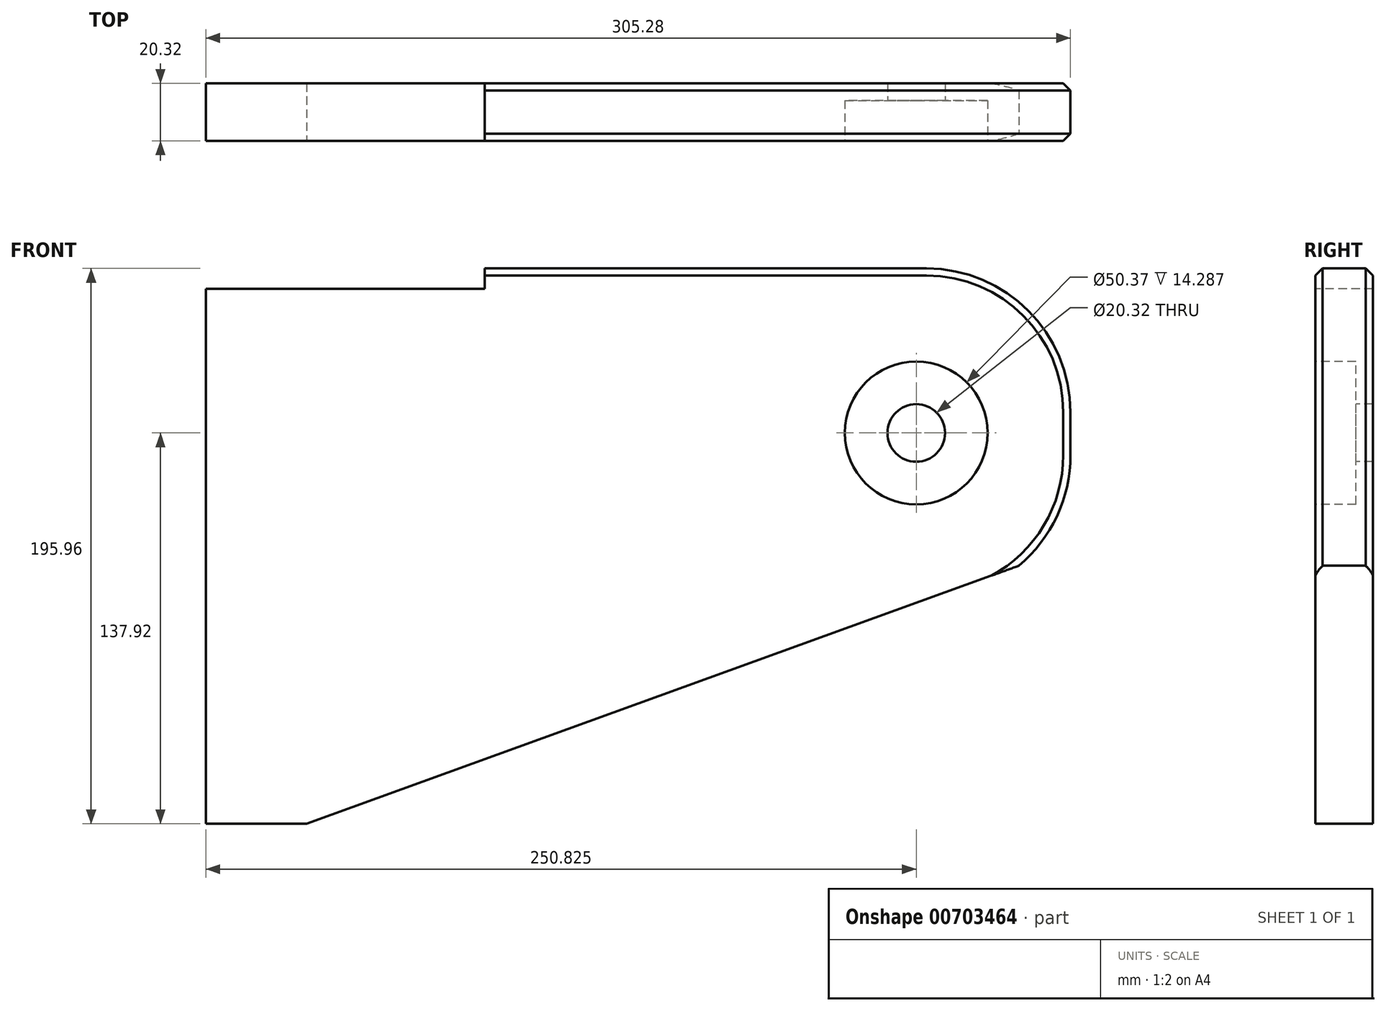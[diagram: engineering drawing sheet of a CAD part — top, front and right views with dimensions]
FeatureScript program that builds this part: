
annotation { "Feature Type Name" : "Feature", "Feature Type Description" : "" }
export const myFeature = defineFeature(function(context is Context, id is Id, definition is map)
    precondition{}
    {
        {
            var Q0;
            Q0=qCreatedBy(makeId("Front.planeOp"),FACE);
            var sketch = newSketch(context, id + "F0", { "sketchPlane" : qUnion([Q0])});
            skLineSegment(sketch, "E0", {"start": v(0, 0) * mm, "end": v(0, -188.72) * mm});
            skLineSegment(sketch, "E1", {"start": v(0, 0) * mm, "end": v(98.43, 0) * mm});
            skLineSegment(sketch, "E2", {"start": v(98.43, 0) * mm, "end": v(98.43, 7.24) * mm});
            skPoint(sketch, "E3", {"position": v(250.83, -50.8) * mm});
            skLineSegment(sketch, "E4", {"start": v(98.43, 7.24) * mm, "end": v(152.88, 7.24) * mm});
            skLineSegment(sketch, "E5", {"start": v(0, -188.72) * mm, "end": v(35.54, -188.72) * mm});
            skCircle(sketch, "E6", {"center": v(250.83, -50.8) * mm, "radius": 25.18 * mm});
            skCircle(sketch, "E7", {"center": v(250.83, -50.8) * mm, "radius": 10.16 * mm});
            skPoint(sketch, "E8.visualSharp", {"position": v(305.28, 7.24) * mm});
            skPoint(sketch, "E9.visualSharp", {"position": v(314.33, -98.03) * mm});
            skLineSegment(sketch, "E10", {"start": v(254.48, 7.24) * mm, "end": v(254.48, 7.24) * mm});
            skLineSegment(sketch, "E11", {"start": v(305.28, -43.56) * mm, "end": v(305.28, -58.64) * mm});
            skLineSegment(sketch, "E12", {"start": v(254.48, -109.44) * mm, "end": v(254.48, -109.44) * mm});
            skPoint(sketch, "E13.visualSharp", {"position": v(305.28, -109.44) * mm});
            skArc(sketch, "E13.filletArc", {"start": v(287, -97.67) * mm, "mid": v(300.48, -80.19) * mm, "end": v(305.28, -58.64) * mm});
            skArc(sketch, "E14.filletArc", {"start": v(305.28, -43.56) * mm, "mid": v(290.4, -7.64) * mm, "end": v(254.48, 7.24) * mm});
            skLineSegment(sketch, "E15", {"start": v(152.88, 7.24) * mm, "end": v(254.48, 7.24) * mm});
            skLineSegment(sketch, "E16", {"start": v(254.48, -109.44) * mm, "end": v(35.54, -188.72) * mm});
            skLineSegment(sketch, "E17", {"start": v(254.48, -109.44) * mm, "end": v(287, -97.67) * mm});
            skPoint(sketch, "E17.endSnap0", {"position": v(290.4, -94.56) * mm});
            skPoint(sketch, "E18.orphan", {"position": v(295.57, -94.56) * mm});
            skSolve(sketch);
        }
        {
            var Q0;
            Q0=makeQuery(id+"F0.imprint","IMPRINT",FACE,{"disambiguationData":[TD([[makeQuery(id+"F0.imprint","IMPRINT",EDGE,{"derivedFrom":sQuery(id+"F0.wireOp",EDGE,"E0")}),1.0]])]});
            var Q1;
            Q1=makeQuery(id+"F0.imprint","IMPRINT",FACE,{"disambiguationData":[TD([[makeQuery(id+"F0.imprint","IMPRINT",EDGE,{"derivedFrom":sQuery(id+"F0.wireOp",EDGE,"E6")}),1.0]])]});
            var Q2;
            Q2=makeQuery(id+"F0.imprint","IMPRINT",FACE,{"disambiguationData":[TD([[makeQuery(id+"F0.imprint","IMPRINT",EDGE,{"derivedFrom":sQuery(id+"F0.wireOp",EDGE,"E7")}),1.0]])]});
            extrude(context, id + "F1", {"entities" : qUnion([Q0, Q1, Q2]), "oppositeDirection" : true, "depth" : 20.32 * mm, "offsetDistance" : 25.4 * mm});
        }
        {
            var Q0;
            Q0=makeQuery(id+"F0.imprint","IMPRINT",FACE,{"disambiguationData":[TD([[makeQuery(id+"F0.imprint","IMPRINT",EDGE,{"derivedFrom":sQuery(id+"F0.wireOp",EDGE,"E6")}),1.0]])]});
            extrude(context, id + "F2", {"entities" : qUnion([Q0]), "operationType" : NewBodyOperationType.REMOVE, "oppositeDirection" : true, "depth" : 14.29 * mm, "offsetDistance" : 25.4 * mm});
        }
        {
            var Q0;
            Q0=makeQuery(id+"F0.imprint","IMPRINT",FACE,{"disambiguationData":[TD([[makeQuery(id+"F0.imprint","IMPRINT",EDGE,{"derivedFrom":sQuery(id+"F0.wireOp",EDGE,"E7")}),1.0]])]});
            extrude(context, id + "F3", {"entities" : qUnion([Q0]), "operationType" : NewBodyOperationType.REMOVE, "oppositeDirection" : true, "depth" : 25.4 * mm, "offsetDistance" : 25.4 * mm});
        }
        {
            var Q0;
            Q0=makeQuery(id+"F1.opExtrude","CAP_EDGE",EDGE,{"disambiguationData":[OSD([sQuery(id+"F0.wireOp",EDGE,"E4"),sQuery(id+"F0.wireOp",EDGE,"E15")])],"isStart":true});
            var Q1;
            Q1=makeQuery(id+"F1.opExtrude","CAP_EDGE",EDGE,{"disambiguationData":[OSD([sQuery(id+"F0.wireOp",EDGE,"E4"),sQuery(id+"F0.wireOp",EDGE,"E15")])],"isStart":false});
            chamfer(context, id + "F4", {"entities" : qUnion([Q0, Q1]), "width" : 2.54 * mm, "tangentPropagation" : true});
        }
    });
